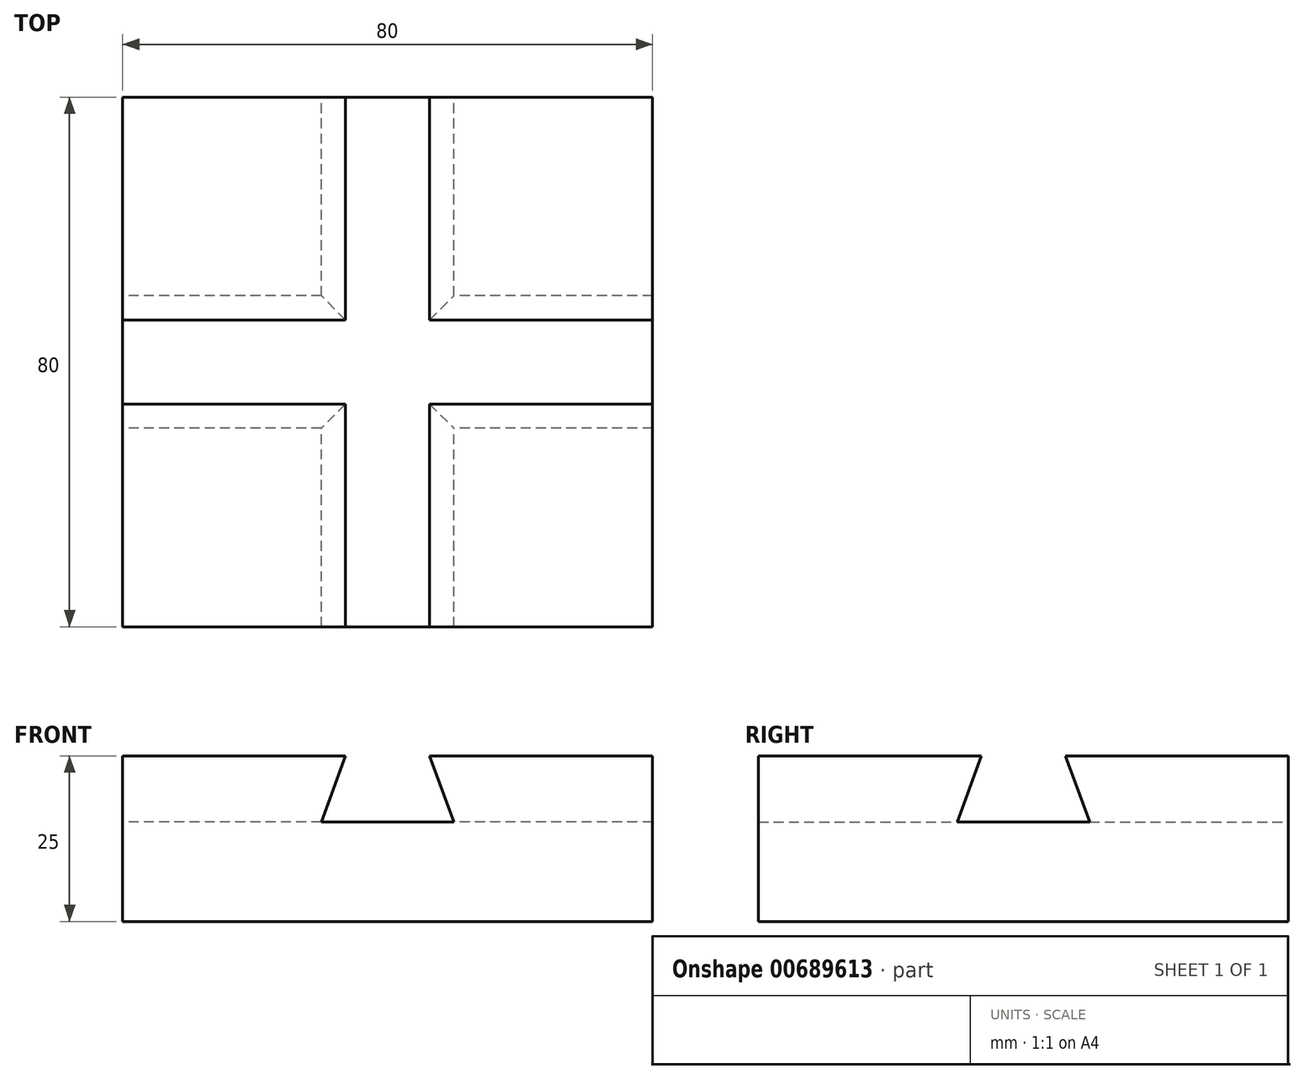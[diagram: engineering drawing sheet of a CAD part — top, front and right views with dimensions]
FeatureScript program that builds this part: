
annotation { "Feature Type Name" : "Feature", "Feature Type Description" : "" }
export const myFeature = defineFeature(function(context is Context, id is Id, definition is map)
    precondition{}
    {
        {
            var Q0;
            Q0=qCreatedBy(makeId("Front.planeOp"),FACE);
            var sketch = newSketch(context, id + "F0", { "sketchPlane" : qUnion([Q0])});
            skLineSegment(sketch, "E0", {"start": v(0, 0) * mm, "end": v(80, 0) * mm});
            skLineSegment(sketch, "E1", {"start": v(80, 0) * mm, "end": v(80, 25) * mm});
            skLineSegment(sketch, "E2", {"start": v(80, 25) * mm, "end": v(0, 25) * mm});
            skLineSegment(sketch, "E3", {"start": v(0, 25) * mm, "end": v(0, 0) * mm});
            skSolve(sketch);
        }
        {
            var Q0;
            Q0=makeQuery(id+"F0.imprint","IMPRINT",FACE,{"disambiguationData":[TD([[makeQuery(id+"F0.imprint","IMPRINT",EDGE,{"derivedFrom":sQuery(id+"F0.wireOp",EDGE,"E0")}),1.0]])]});
            extrude(context, id + "F1", {"entities" : qUnion([Q0]), "depth" : 80 * mm, "offsetDistance" : 25 * mm});
        }
        {
            var Q0;
            Q0=qCreatedBy(makeId("Right.planeOp"),FACE);
            var sketch = newSketch(context, id + "F2", { "sketchPlane" : qUnion([Q0])});
            skLineSegment(sketch, "E4", {"start": v(0, 0) * mm, "end": v(-40, 0) * mm, "construction": true});
            skLineSegment(sketch, "E5", {"start": v(-30, 15) * mm, "end": v(-33.64, 25) * mm});
            skLineSegment(sketch, "E6", {"start": v(-33.64, 25) * mm, "end": v(-46.36, 25) * mm});
            skLineSegment(sketch, "E7", {"start": v(-50, 15) * mm, "end": v(-46.36, 25) * mm});
            skLineSegment(sketch, "E8", {"start": v(-50, 15) * mm, "end": v(-30, 15) * mm});
            skSolve(sketch);
        }
        {
            var Q0;
            Q0=makeQuery(id+"F2.imprint","IMPRINT",FACE,{"disambiguationData":[TD([[makeQuery(id+"F2.imprint","IMPRINT",EDGE,{"derivedFrom":sQuery(id+"F2.wireOp",EDGE,"E5")}),1.0]])]});
            extrude(context, id + "F3", {"entities" : qUnion([Q0]), "operationType" : NewBodyOperationType.REMOVE, "depth" : 80 * mm, "offsetDistance" : 25 * mm});
        }
        {
            var Q0;
            Q0=qCreatedBy(makeId("Front.planeOp"),FACE);
            var sketch = newSketch(context, id + "F4", { "sketchPlane" : qUnion([Q0])});
            skLineSegment(sketch, "E9", {"start": v(40, 25) * mm, "end": v(46.36, 25) * mm});
            skLineSegment(sketch, "E10", {"start": v(40, 25) * mm, "end": v(33.64, 25) * mm});
            skLineSegment(sketch, "E11", {"start": v(40, 15) * mm, "end": v(50, 15) * mm});
            skLineSegment(sketch, "E12", {"start": v(40, 15) * mm, "end": v(30, 15) * mm});
            skLineSegment(sketch, "E13", {"start": v(30, 15) * mm, "end": v(33.64, 25) * mm});
            skLineSegment(sketch, "E14", {"start": v(50, 15) * mm, "end": v(46.36, 25) * mm});
            skSolve(sketch);
        }
        {
            var Q0;
            Q0=makeQuery(id+"F4.imprint","IMPRINT",FACE,{"disambiguationData":[TD([[makeQuery(id+"F4.imprint","IMPRINT",EDGE,{"derivedFrom":sQuery(id+"F4.wireOp",EDGE,"E9")}),-1.0]])]});
            extrude(context, id + "F5", {"entities" : qUnion([Q0]), "operationType" : NewBodyOperationType.REMOVE, "depth" : 80 * mm, "offsetDistance" : 25 * mm});
        }
    });
